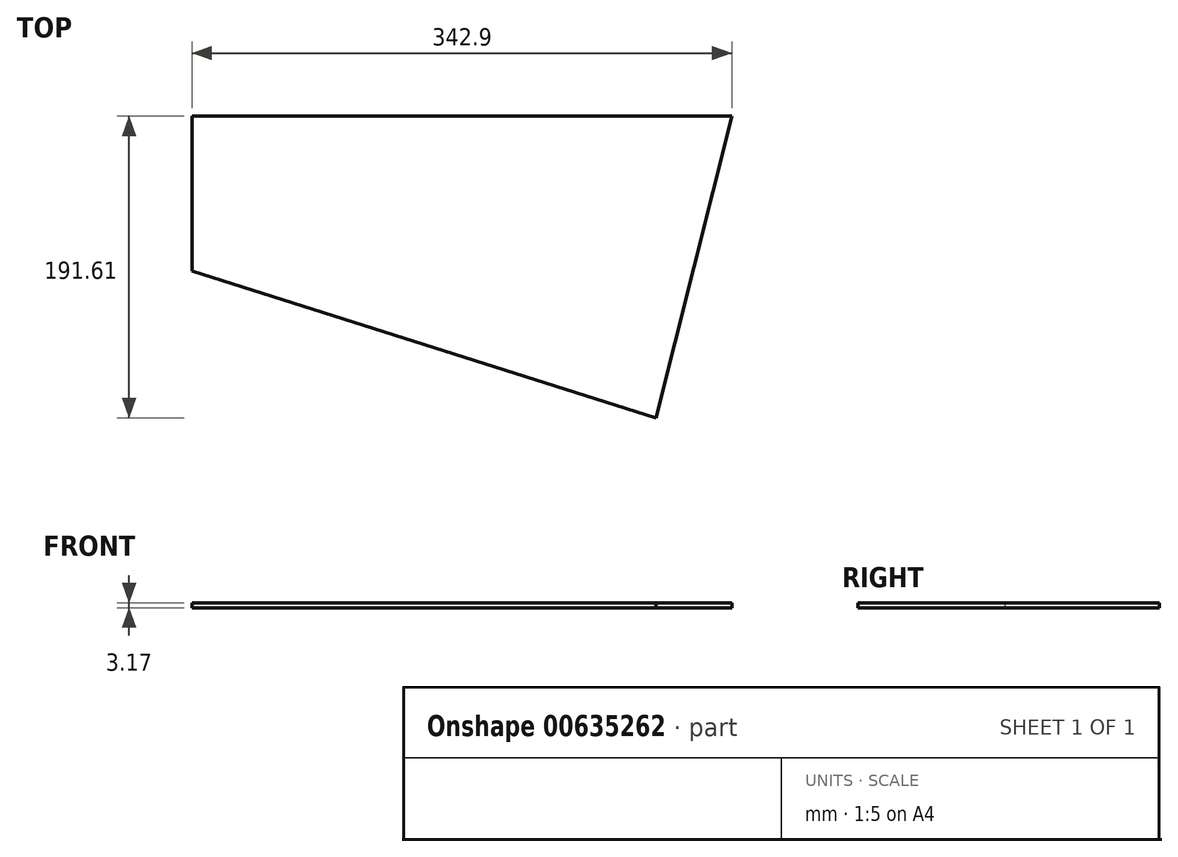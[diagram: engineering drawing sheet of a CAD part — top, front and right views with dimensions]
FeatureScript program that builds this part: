
annotation { "Feature Type Name" : "Feature", "Feature Type Description" : "" }
export const myFeature = defineFeature(function(context is Context, id is Id, definition is map)
    precondition{}
    {
        {
            var Q0;
            Q0=qCreatedBy(makeId("Top.planeOp"),FACE);
            var sketch = newSketch(context, id + "F0", { "sketchPlane" : qUnion([Q0])});
            skLineSegment(sketch, "E0", {"start": v(0, 0) * mm, "end": v(-48.32, -191.61) * mm});
            skLineSegment(sketch, "E1", {"start": v(-48.32, -191.61) * mm, "end": v(-342.9, -98.26) * mm});
            skLineSegment(sketch, "E2", {"start": v(-342.9, -98.26) * mm, "end": v(-342.9, 0) * mm});
            skLineSegment(sketch, "E3", {"start": v(-342.9, 0) * mm, "end": v(0, 0) * mm});
            skSolve(sketch);
        }
        {
            var Q0;
            Q0 = qSketchRegion(id + "F0", true);
            extrude(context, id + "F1", {"entities" : qUnion([Q0]), "depth" : 3.17 * mm, "offsetDistance" : 25.4 * mm});
        }
    });
